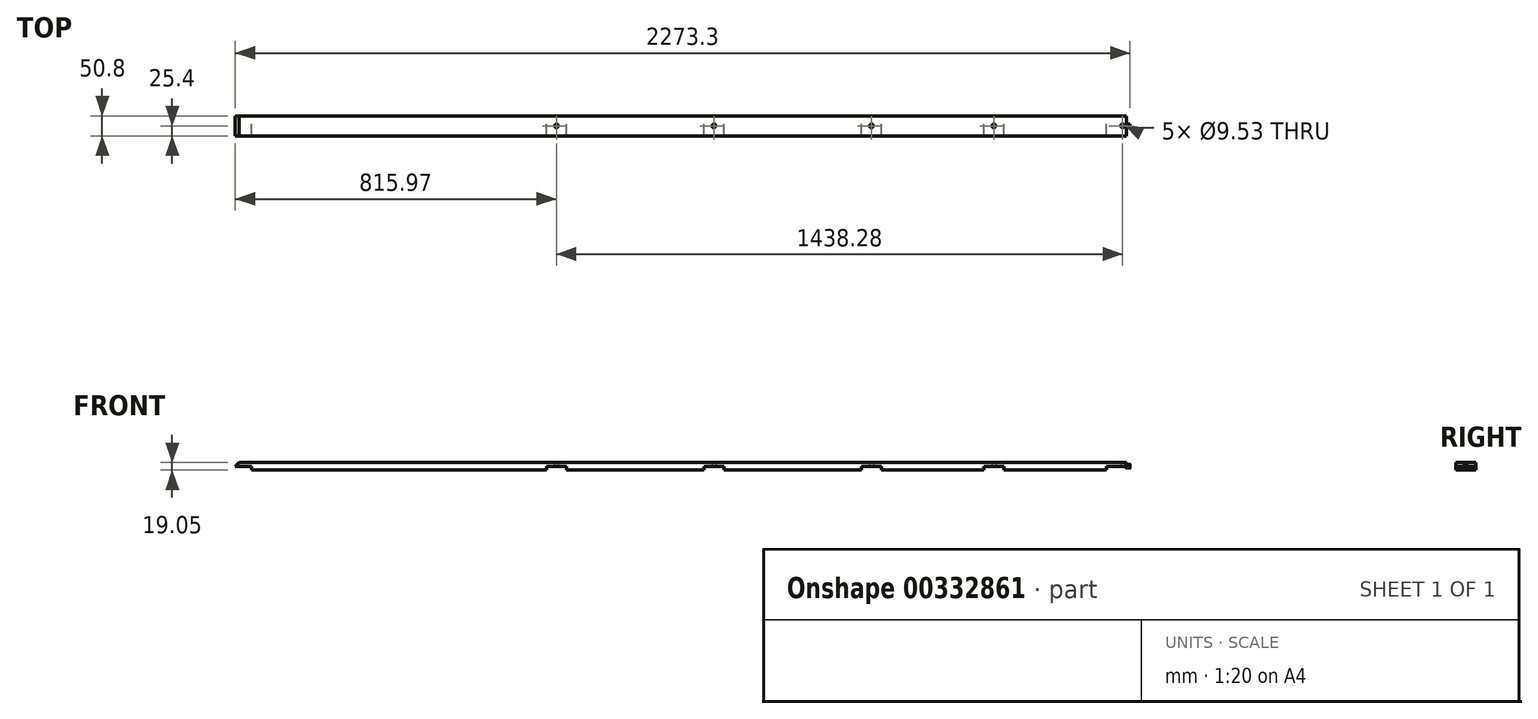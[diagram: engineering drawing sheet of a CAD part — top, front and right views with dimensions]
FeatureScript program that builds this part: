
annotation { "Feature Type Name" : "Feature", "Feature Type Description" : "" }
export const myFeature = defineFeature(function(context is Context, id is Id, definition is map)
    precondition{}
    {
        {
            var Q0;
            Q0=qCreatedBy(makeId("Front.planeOp"),FACE);
            var sketch = newSketch(context, id + "F0", { "sketchPlane" : qUnion([Q0])});
            skLineSegment(sketch, "E0.right", {"start": v(2273.3, 9.53) * mm, "end": v(2273.3, 19.05) * mm});
            skLineSegment(sketch, "E1", {"start": v(2273.3, 19.05) * mm, "end": v(1962.15, 19.05) * mm});
            skPoint(sketch, "E2.left.start.orphan", {"position": v(-798.41, -3.82) * mm});
            skLineSegment(sketch, "E3.top", {"start": v(800.1, 9.52) * mm, "end": v(850.9, 9.52) * mm});
            skLineSegment(sketch, "E3.left", {"start": v(800.1, 0) * mm, "end": v(800.1, 9.52) * mm});
            skLineSegment(sketch, "E3.right", {"start": v(850.9, 0) * mm, "end": v(850.9, 9.52) * mm});
            skLineSegment(sketch, "E4.trimOffspring", {"start": v(850.9, 0) * mm, "end": v(1200.15, 0) * mm});
            skLineSegment(sketch, "E5.top", {"start": v(1600.2, 9.52) * mm, "end": v(1651, 9.52) * mm});
            skLineSegment(sketch, "E5.left", {"start": v(1600.2, 0) * mm, "end": v(1600.2, 9.52) * mm});
            skLineSegment(sketch, "E5.right", {"start": v(1651, 0) * mm, "end": v(1651, 9.52) * mm});
            skLineSegment(sketch, "E6.trimOffspring", {"start": v(1651, 0) * mm, "end": v(1911.35, 0) * mm});
            skLineSegment(sketch, "E7.top", {"start": v(2222.5, 9.53) * mm, "end": v(2273.3, 9.53) * mm});
            skLineSegment(sketch, "E7.left", {"start": v(2222.5, 0) * mm, "end": v(2222.5, 9.53) * mm});
            skPoint(sketch, "E8.orphan", {"position": v(2273.3, 0) * mm});
            skLineSegment(sketch, "E9", {"start": v(9.52, 9.52) * mm, "end": v(19.05, 19.05) * mm});
            skLineSegment(sketch, "E10.trimOffspring", {"start": v(50.8, 0) * mm, "end": v(800.1, 0) * mm});
            skLineSegment(sketch, "E11.top", {"start": v(9.52, 9.52) * mm, "end": v(50.8, 9.52) * mm});
            skLineSegment(sketch, "E11.right", {"start": v(50.8, 0) * mm, "end": v(50.8, 9.52) * mm});
            skPoint(sketch, "E12.orphan", {"position": v(0, 0) * mm});
            skPoint(sketch, "E13.left.start.orphan", {"position": v(609.6, 9.52) * mm});
            skLineSegment(sketch, "E14", {"start": v(1936.75, 0) * mm, "end": v(1936.75, -146.1) * mm, "construction": true});
            skLineSegment(sketch, "E15.left", {"start": v(1962.15, 9.53) * mm, "end": v(1962.15, 0) * mm});
            skLineSegment(sketch, "E15.right", {"start": v(1911.35, 9.53) * mm, "end": v(1911.35, 0) * mm});
            skPoint(sketch, "E15.middle", {"position": v(1936.75, 0) * mm});
            skPoint(sketch, "E16.orphan", {"position": v(1962.15, -9.52) * mm});
            skPoint(sketch, "E17.orphan", {"position": v(1911.35, -9.52) * mm});
            skLineSegment(sketch, "E18.trimOffspring", {"start": v(1936.75, 0) * mm, "end": v(2222.5, 0) * mm});
            skLineSegment(sketch, "E19.trimOffspring", {"start": v(1911.35, 19.05) * mm, "end": v(19.05, 19.05) * mm});
            skLineSegment(sketch, "E20", {"start": v(1911.35, 9.53) * mm, "end": v(1962.15, 9.52) * mm});
            skLineSegment(sketch, "E21", {"start": v(1911.35, 19.05) * mm, "end": v(1962.15, 19.05) * mm});
            skLineSegment(sketch, "E22.bottom", {"start": v(1250.95, 9.52) * mm, "end": v(1200.15, 9.53) * mm});
            skLineSegment(sketch, "E22.left", {"start": v(1250.95, 9.52) * mm, "end": v(1250.95, 0) * mm});
            skLineSegment(sketch, "E22.right", {"start": v(1200.15, 9.52) * mm, "end": v(1200.15, 0) * mm});
            skPoint(sketch, "E22.middle", {"position": v(1225.55, 0) * mm});
            skLineSegment(sketch, "E23.trimOffspring", {"start": v(1250.95, 0) * mm, "end": v(1600.2, 0) * mm});
            skPoint(sketch, "E24.orphan", {"position": v(1200.15, -9.52) * mm});
            skPoint(sketch, "E25.orphan", {"position": v(1250.95, -9.53) * mm});
            skSolve(sketch);
        }
        {
            var Q0;
            Q0=qSketchRegion(id+"F0",true);
            extrude(context, id + "F1", {"entities" : qUnion([Q0]), "depth" : 50.8 * mm});
        }
        {
            var Q0;
            Q0=qCreatedBy(makeId("Right.planeOp"),FACE);
            cPlane(context, id + "F2", {"entities" : qUnion([Q0]), "cplaneType" : CPlaneType.OFFSET, "offset" : 2273.3 * mm, "width" : 152.4 * mm, "height" : 152.4 * mm});
        }
        {
            var Q0;
            Q0=qCreatedBy(id+"F2.planeOp",FACE);
            var sketch = newSketch(context, id + "F3", { "sketchPlane" : qUnion([Q0])});
            skCircle(sketch, "E26", {"center": v(-25.4, 9.53) * mm, "radius": 4.76 * mm});
            skSolve(sketch);
        }
        {
            var Q0;
            Q0=qSketchRegion(id+"F3",true);
            extrude(context, id + "F4", {"entities" : qUnion([Q0]), "operationType" : NewBodyOperationType.ADD, "depth" : 9.52 * mm});
        }
        {
            var Q0;
            Q0=qCreatedBy(makeId("Top.planeOp"),FACE);
            cPlane(context, id + "F5", {"entities" : qUnion([Q0]), "cplaneType" : CPlaneType.OFFSET, "offset" : 9.52 * mm, "width" : 152.4 * mm, "height" : 152.4 * mm});
        }
        {
            var Q0;
            Q0=qCreatedBy(id+"F5.planeOp",FACE);
            var sketch = newSketch(context, id + "F6", { "sketchPlane" : qUnion([Q0])});
            skCircle(sketch, "E27", {"center": v(825.5, -25.4) * mm, "radius": 4.76 * mm});
            skCircle(sketch, "E28", {"center": v(1625.6, -25.4) * mm, "radius": 4.76 * mm});
            skPoint(sketch, "E29.center.orphan", {"position": v(1625.6, -243.48) * mm});
            skCircle(sketch, "E30", {"center": v(2263.78, -25.4) * mm, "radius": 4.76 * mm});
            skCircle(sketch, "E31", {"center": v(1936.75, -25.4) * mm, "radius": 4.76 * mm});
            skCircle(sketch, "E32", {"center": v(1225.55, -25.4) * mm, "radius": 4.76 * mm});
            skSolve(sketch);
        }
        {
            var Q0;
            Q0=qSketchRegion(id+"F6",true);
            extrude(context, id + "F7", {"entities" : qUnion([Q0]), "operationType" : NewBodyOperationType.REMOVE, "depth" : 19.05 * mm});
        }
    });
